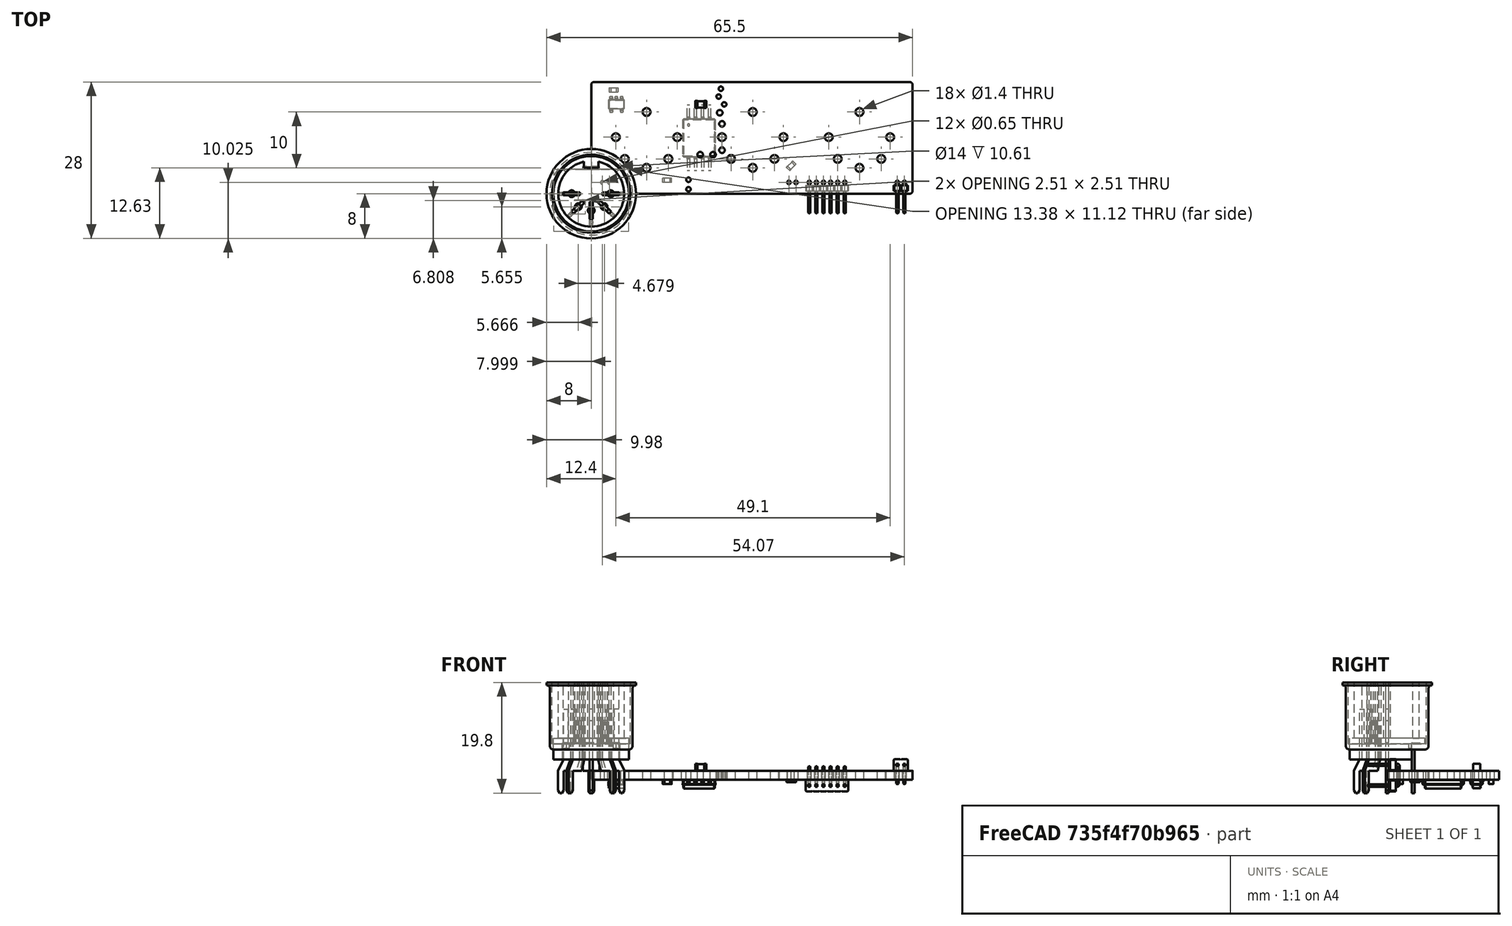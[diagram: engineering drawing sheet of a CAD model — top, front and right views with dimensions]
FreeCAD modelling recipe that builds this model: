
FCSTD DOCUMENT  (FreeCAD 0.20R27422 (Git))
Label: Ultra-midi
License: All rights reserved
LicenseURL: http://en.wikipedia.org/wiki/All_rights_reserved
objects: Part::Feature×30, App::Link×16, App::Part×8, PartDesign::CoordinateSystem×1, Sketcher::SketchObject×1
note: 32 computed .brp shape members not serialized (recipe doc carries the construction recipe); baked Part::Feature solids carry a one-line shape summary decoded from their .brp

FEATURE [PartDesign::CoordinateSystem] Local_CS_69dd
  AttacherType = Attacher::AttachEngine3D
FEATURE [Part::Feature] Pcb_69dd
  Placement = pos=(-116,98,0) rot=(0,0,1;0rad)
  shape: bbox 57.5 x 20 x 1.6 mm, 50 faces (baked)
FEATURE [Sketcher::SketchObject] PCB_Sketch_69dd
  FullyConstrained = false
  sketch-geometry (18):
    g0: LineSegment StartX=57 StartY=20 StartZ=0 EndX=0.5 EndY=20 EndZ=0
    g1: LineSegment StartX=8e-16 StartY=19.5 StartZ=0 EndX=0 EndY=0.5 EndZ=0
    g2: LineSegment StartX=57.5 StartY=0.5 StartZ=0 EndX=57.5 EndY=19.5 EndZ=0
    g3: LineSegment StartX=0.5 StartY=0 StartZ=0 EndX=57 EndY=-1.3e-15 EndZ=0
    g4: ArcOfCircle CenterX=57 CenterY=0.500001 CenterZ=0 NormalX=0 NormalY=0 NormalZ=-1 AngleXU=-3.14159 Radius=0.500001 StartAngle=0 EndAngle=1.57079
    g5: ArcOfCircle CenterX=0.500001 CenterY=19.5 CenterZ=0 NormalX=0 NormalY=0 NormalZ=-1 AngleXU=2.66714e-06 Radius=0.500001 StartAngle=0 EndAngle=1.57079
    g6: ArcOfCircle CenterX=0.500001 CenterY=0.500001 CenterZ=0 NormalX=0 NormalY=0 NormalZ=-1 AngleXU=-1.57079 Radius=0.500001 StartAngle=0 EndAngle=1.57079
    g7: ArcOfCircle CenterX=57 CenterY=19.5 CenterZ=0 NormalX=0 NormalY=0 NormalZ=-1 AngleXU=1.5708 Radius=0.500001 StartAngle=0 EndAngle=1.57079
    g8: Circle CenterX=19.5 CenterY=7 CenterZ=0 NormalX=0 NormalY=0 NormalZ=1 AngleXU=0 Radius=0.5
    g9: Circle CenterX=17.4 CenterY=2.5 CenterZ=0 NormalX=0 NormalY=0 NormalZ=1 AngleXU=0 Radius=0.4
    g10: Circle CenterX=23.4 CenterY=7.8 CenterZ=0 NormalX=0 NormalY=0 NormalZ=1 AngleXU=0 Radius=0.5
    g11: Circle CenterX=23.2 CenterY=18.8 CenterZ=0 NormalX=0 NormalY=0 NormalZ=1 AngleXU=0 Radius=0.4
    g12: Circle CenterX=22.8 CenterY=17.4 CenterZ=0 NormalX=0 NormalY=0 NormalZ=1 AngleXU=0 Radius=0.4
    g13: Circle CenterX=23 CenterY=14.5 CenterZ=0 NormalX=0 NormalY=0 NormalZ=1 AngleXU=0 Radius=0.5
    g14: Circle CenterX=23.4 CenterY=12.5 CenterZ=0 NormalX=0 NormalY=0 NormalZ=1 AngleXU=0 Radius=0.5
    g15: Circle CenterX=17.4 CenterY=0.8 CenterZ=0 NormalX=0 NormalY=0 NormalZ=1 AngleXU=0 Radius=0.4
    g16: Circle CenterX=23.8 CenterY=16 CenterZ=0 NormalX=0 NormalY=0 NormalZ=1 AngleXU=0 Radius=0.4
    g17: Circle CenterX=21.8 CenterY=7 CenterZ=0 NormalX=0 NormalY=0 NormalZ=1 AngleXU=0 Radius=0.5
  constraints (8):
    c: Coincident(g1,g6)
    c: Coincident(g1,g5)
    c: Coincident(g3,g6)
    c: Coincident(g0,g5)
    c: Coincident(g3,g4)
    c: Coincident(g0,g7)
    c: Coincident(g2,g4)
    c: Coincident(g2,g7)
FEATURE [App::Part] Board_Geoms_69dd
  Group = -> [Local_CS_69dd,Pcb_69dd,PCB_Sketch_69dd]
  Origin = -> Origin
FEATURE [Part::Feature] Shape  label="J2_PinHeader_1x02_P127mm_Horizontal_337eb045ee12"
  Placement = pos=(56.05,2.025,0) rot=(0,0,-1;1.5708rad)
  shape: bbox 2.54 x 5.7 x 4.5 mm, 58 faces (baked)
FEATURE [Part::Feature] Shape001  label="C6_C_0805_2012Metric_c09b5ff471bc"
  Placement = pos=(19.6,16,0) rot=(0,0,1;0rad)
  shape: bbox 2 x 1.25 x 1.25 mm, 28 faces (baked)
FEATURE [App::Link] J2_PinHeader_1x02_P127mm_Horizontal_337eb045ee12_ln_  label="J1_PinHeader_1x02_P127mm_Horizontal_ae3b6cd6d5c1"
  LinkPlacement = pos=(3.25,2.025,0) rot=(0,0,-1;1.5708rad)
  LinkedObject = -> Shape
  Placement = pos=(3.25,2.025,0) rot=(0,0,-1;1.5708rad)
FEATURE [App::Link] J2_PinHeader_1x02_P127mm_Horizontal_337eb045ee12_ln_001  label="J3_PinHeader_1x02_P127mm_Horizontal_27ee44c8c3d4"
  LinkPlacement = pos=(36.65,2.025,0) rot=(0,0,-1;1.5708rad)
  LinkedObject = -> Shape
  Placement = pos=(36.65,2.025,0) rot=(0,0,-1;1.5708rad)
FEATURE [Part::Feature] Shape002  label="FB3_L_0603_1608Metric_df2c29076625"
  Placement = pos=(13.6,2.4,-1.6) rot=(0,1,0;3.14159rad)
  shape: bbox 1.6 x 0.8 x 0.8 mm, 28 faces (baked)
FEATURE [Part::Feature] Shape003  label="C5_C_0603_1608Metric_0867c8c5745e"
  Placement = pos=(4,18.6,-1.6) rot=(1,0,0;3.14159rad)
  shape: bbox 1.6 x 0.8 x 0.8 mm, 28 faces (baked)
FEATURE [Part::Feature] Shape004  label="R5_R_0603_1608Metric_8c8bab43711c"
  Placement = pos=(35.8,5,-1.6) rot=(0.92388,0.382683,0;3.14159rad)
  shape: bbox 1.697 x 1.697 x 0.45 mm, 26 faces (baked)
FEATURE [Part::Feature] Shape005  label="J4_PinHeader_1x06_P127mm_Horizontal_489f8f595e1f"
  Placement = pos=(39.025,2.025,-1.6) rot=(0.707107,-0.707107,0;3.14159rad)
  shape: bbox 7.62 x 5.7 x 4.5 mm, 166 faces (baked)
FEATURE [App::Link] FB3_L_0603_1608Metric_df2c29076625_ln_  label="FB1_L_0603_1608Metric_149065dd4c7b"
  LinkPlacement = pos=(36,7.4,-1.6) rot=(0.92388,0.382683,0;3.14159rad)
  LinkedObject = -> Shape002
  Placement = pos=(36,7.4,-1.6) rot=(0.92388,0.382683,0;3.14159rad)
FEATURE [Part::Feature] Shape006  label="U1_SSO_8_68x59mm_P127mm_Clearance8mm_cd01ce0f9bbe"
  Placement = pos=(19.3,10,-1.6) rot=(0.707107,-0.707107,0;3.14159rad)
  shape: bbox 5.9 x 11.7 x 1.6 mm, 156 faces (baked)
FEATURE [Part::Feature] Shape007  label="U2_SOT_23_5_2942c334eb8a"
  Placement = pos=(4.5,16,-1.6) rot=(0.707107,-0.707107,0;3.14159rad)
  shape: bbox 2.9 x 2.8 x 1.55 mm, 109 faces (baked)
FEATURE [App::Link] R5_R_0603_1608Metric_8c8bab43711c_ln_  label="R4_R_0603_1608Metric_3ff6b89587b2"
  LinkPlacement = pos=(8,10,-1.6) rot=(0.707107,0.707107,0;3.14159rad)
  LinkedObject = -> Shape004
  Placement = pos=(8,10,-1.6) rot=(0.707107,0.707107,0;3.14159rad)
FEATURE [App::Link] C5_C_0603_1608Metric_0867c8c5745e_ln_  label="C2_C_0603_1608Metric_22715801060e"
  LinkPlacement = pos=(10.8,8.2,-1.6) rot=(1,0,0;3.14159rad)
  LinkedObject = -> Shape003
  Placement = pos=(10.8,8.2,-1.6) rot=(1,0,0;3.14159rad)
FEATURE [App::Link] C6_C_0805_2012Metric_c09b5ff471bc_ln_  label="C4_C_0805_2012Metric_26a949b8cd84"
  LinkPlacement = pos=(1.8,13,-1.6) rot=(0.707107,0.707107,0;3.14159rad)
  LinkedObject = -> Shape001
  Placement = pos=(1.8,13,-1.6) rot=(0.707107,0.707107,0;3.14159rad)
FEATURE [App::Link] R5_R_0603_1608Metric_8c8bab43711c_ln_001  label="R2_R_0603_1608Metric_4e10fd813094"
  LinkPlacement = pos=(49.5,16.5,-1.6) rot=(0.92388,-0.382683,0;3.14159rad)
  LinkedObject = -> Shape004
  Placement = pos=(49.5,16.5,-1.6) rot=(0.92388,-0.382683,0;3.14159rad)
FEATURE [App::Link] FB3_L_0603_1608Metric_df2c29076625_ln_001  label="FB2_L_0603_1608Metric_fe7989b07d85"
  LinkPlacement = pos=(12.8,12.2,-1.6) rot=(0.707107,0.707107,0;3.14159rad)
  LinkedObject = -> Shape002
  Placement = pos=(12.8,12.2,-1.6) rot=(0.707107,0.707107,0;3.14159rad)
FEATURE [App::Link] C5_C_0603_1608Metric_0867c8c5745e_ln_001  label="C1_C_0603_1608Metric_b41121d6c93c"
  LinkPlacement = pos=(46.2,16.3,-1.6) rot=(0.92388,0.382683,0;3.14159rad)
  LinkedObject = -> Shape003
  Placement = pos=(46.2,16.3,-1.6) rot=(0.92388,0.382683,0;3.14159rad)
FEATURE [App::Link] R5_R_0603_1608Metric_8c8bab43711c_ln_002  label="R7_R_0603_1608Metric_dfa80113c302"
  LinkPlacement = pos=(27,1.8,-1.6) rot=(0,1,0;3.14159rad)
  LinkedObject = -> Shape004
  Placement = pos=(27,1.8,-1.6) rot=(0,1,0;3.14159rad)
FEATURE [App::Link] FB3_L_0603_1608Metric_df2c29076625_ln_002  label="FB4_L_0603_1608Metric_f99d6db0d256"
  LinkPlacement = pos=(54.8,6.2,-1.6) rot=(0.707107,-0.707107,0;3.14159rad)
  LinkedObject = -> Shape002
  Placement = pos=(54.8,6.2,-1.6) rot=(0.707107,-0.707107,0;3.14159rad)
FEATURE [App::Link] FB3_L_0603_1608Metric_df2c29076625_ln_003  label="FB5_L_0603_1608Metric_030844127197"
  LinkPlacement = pos=(25,3.4,-1.6) rot=(0,1,0;3.14159rad)
  LinkedObject = -> Shape002
  Placement = pos=(25,3.4,-1.6) rot=(0,1,0;3.14159rad)
FEATURE [App::Link] R5_R_0603_1608Metric_8c8bab43711c_ln_003  label="R3_R_0603_1608Metric_b0f0240fa3c2"
  LinkPlacement = pos=(14.6,14.8,-1.6) rot=(0,1,0;3.14159rad)
  LinkedObject = -> Shape004
  Placement = pos=(14.6,14.8,-1.6) rot=(0,1,0;3.14159rad)
FEATURE [App::Link] R5_R_0603_1608Metric_8c8bab43711c_ln_004  label="R6_R_0603_1608Metric_639142cc7455"
  LinkPlacement = pos=(33.2,14.6,-1.6) rot=(0,1,0;3.14159rad)
  LinkedObject = -> Shape004
  Placement = pos=(33.2,14.6,-1.6) rot=(0,1,0;3.14159rad)
FEATURE [App::Link] R5_R_0603_1608Metric_8c8bab43711c_ln_005  label="R1_R_0603_1608Metric_cbd55fb59e40"
  LinkPlacement = pos=(53.2,3,-1.6) rot=(0.707107,0.707107,0;3.14159rad)
  LinkedObject = -> Shape004
  Placement = pos=(53.2,3,-1.6) rot=(0.707107,0.707107,0;3.14159rad)
FEATURE [App::Link] C5_C_0603_1608Metric_0867c8c5745e_ln_002  label="C3_C_0603_1608Metric_cf41ac51516b"
  LinkPlacement = pos=(33.1375,16.2,-1.6) rot=(1,0,0;3.14159rad)
  LinkedObject = -> Shape003
  Placement = pos=(33.1375,16.2,-1.6) rot=(1,0,0;3.14159rad)
FEATURE [App::Part] Bot_69dd
  Group = -> [Shape002,Shape003,Shape004,Shape005,FB3_L_0603_1608Metric_df2c29076625_ln_,Shape006,Shape007,R5_R_0603_1608Metric_8c8bab43711c_ln_,C5_C_0603_1608Metric_0867c8c5745e_ln_,C6_C_0805_2012Metric_c09b5ff471bc_ln_,R5_R_0603_1608Metric_8c8bab43711c_ln_001,FB3_L_0603_1608Metric_df2c29076625_ln_001,C5_C_0603_1608Metric_0867c8c5745e_ln_001,R5_R_0603_1608Metric_8c8bab43711c_ln_002,+6 more]
  Origin = -> Origin004
FEATURE [Part::Feature] Part__Feature  label="Casing"
  shape: bbox 18.09 x 18.09 x 19.8 mm, 30 faces (baked)
FEATURE [Part::Feature] Part__Feature001  label="Plastic"
  Placement = pos=(0,0,0) rot=(0,0,1;1.5708rad)
  shape: bbox 13.5 x 13.5 x 13.8 mm, 83 faces (baked)
FEATURE [Part::Feature] Part__Feature002  label="Pin-contact1"
  Placement = pos=(0,0,-4) rot=(0,0,1;0rad)
  shape: bbox 3.9 x 0.55 x 15 mm, 20 faces (baked)
FEATURE [Part::Feature] Part__Feature003  label="Pin-contact002"
  Placement = pos=(0,0,-4) rot=(0,0,1;1.5708rad)
  shape: bbox 0.55 x 3.9 x 15 mm, 20 faces (baked)
FEATURE [Part::Feature] Part__Feature004  label="Pin-contact003"
  Placement = pos=(0,0,-4) rot=(0,0,1;3.14159rad)
  shape: bbox 3.9 x 0.55 x 15 mm, 20 faces (baked)
FEATURE [Part::Feature] Part__Feature005  label="Pin-contact004"
  Placement = pos=(0,0,-4) rot=(0,0,1;0.785398rad)
  shape: bbox 3.147 x 3.147 x 15 mm, 20 faces (baked)
FEATURE [Part::Feature] Part__Feature006  label="Pin-contact005"
  Placement = pos=(0,0,-4) rot=(0,0,1;2.35619rad)
  shape: bbox 3.147 x 3.147 x 15 mm, 20 faces (baked)
FEATURE [App::Part] CUI_SD_50BV
  Group = -> [Part__Feature,Part__Feature001,Part__Feature002,Part__Feature003,Part__Feature004,Part__Feature005,Part__Feature006]
  Origin = -> Origin005
  Placement = pos=(9.9,10,0) rot=(0,0,1;0rad)
FEATURE [Part::Feature] Part__Feature007  label="Casing001"
  shape: bbox 18.09 x 18.09 x 19.8 mm, 30 faces (baked)
FEATURE [Part::Feature] Part__Feature008  label="Pin-contact006"
  Placement = pos=(0,0,-4) rot=(0,0,1;1.5708rad)
  shape: bbox 0.55 x 3.9 x 15 mm, 20 faces (baked)
FEATURE [Part::Feature] Part__Feature009  label="Pin-contact007"
  Placement = pos=(0,0,-4) rot=(0,0,1;0rad)
  shape: bbox 3.9 x 0.55 x 15 mm, 20 faces (baked)
FEATURE [Part::Feature] Part__Feature010  label="Plastic001"
  Placement = pos=(0,0,0) rot=(0,0,1;1.5708rad)
  shape: bbox 13.5 x 13.5 x 13.8 mm, 83 faces (baked)
FEATURE [Part::Feature] Part__Feature011  label="Pin-contact008"
  Placement = pos=(0,0,-4) rot=(0,0,1;3.14159rad)
  shape: bbox 3.9 x 0.55 x 15 mm, 20 faces (baked)
FEATURE [Part::Feature] Part__Feature012  label="Pin-contact009"
  Placement = pos=(0,0,-4) rot=(0,0,1;0.785398rad)
  shape: bbox 3.147 x 3.147 x 15 mm, 20 faces (baked)
FEATURE [Part::Feature] Part__Feature013  label="Pin-contact010"
  Placement = pos=(0,0,-4) rot=(0,0,1;2.35619rad)
  shape: bbox 3.147 x 3.147 x 15 mm, 20 faces (baked)
FEATURE [App::Part] CUI_SD_50BV001
  Group = -> [Part__Feature007,Part__Feature010,Part__Feature009,Part__Feature008,Part__Feature011,Part__Feature012,Part__Feature013]
  Origin = -> Origin006
  Placement = pos=(28.9,10,0) rot=(0,0,1;0rad)
FEATURE [Part::Feature] Part__Feature014  label="Casing002"
  shape: bbox 18.09 x 18.09 x 19.8 mm, 30 faces (baked)
FEATURE [Part::Feature] Part__Feature015  label="Pin-contact011"
  Placement = pos=(0,0,-4) rot=(0,0,1;1.5708rad)
  shape: bbox 0.55 x 3.9 x 15 mm, 20 faces (baked)
FEATURE [Part::Feature] Part__Feature016  label="Pin-contact012"
  Placement = pos=(0,0,-4) rot=(0,0,1;0rad)
  shape: bbox 3.9 x 0.55 x 15 mm, 20 faces (baked)
FEATURE [Part::Feature] Part__Feature017  label="Plastic002"
  Placement = pos=(0,0,0) rot=(0,0,1;1.5708rad)
  shape: bbox 13.5 x 13.5 x 13.8 mm, 83 faces (baked)
FEATURE [Part::Feature] Part__Feature018  label="Pin-contact013"
  Placement = pos=(0,0,-4) rot=(0,0,1;3.14159rad)
  shape: bbox 3.9 x 0.55 x 15 mm, 20 faces (baked)
FEATURE [Part::Feature] Part__Feature019  label="Pin-contact014"
  Placement = pos=(0,0,-4) rot=(0,0,1;0.785398rad)
  shape: bbox 3.147 x 3.147 x 15 mm, 20 faces (baked)
FEATURE [Part::Feature] Part__Feature020  label="Pin-contact015"
  Placement = pos=(0,0,-4) rot=(0,0,1;2.35619rad)
  shape: bbox 3.147 x 3.147 x 15 mm, 20 faces (baked)
FEATURE [App::Part] CUI_SD_50BV002
  Group = -> [Part__Feature014,Part__Feature017,Part__Feature016,Part__Feature015,Part__Feature018,Part__Feature019,Part__Feature020]
  Origin = -> Origin007
  Placement = pos=(48,10,0) rot=(0,0,1;0rad)
FEATURE [App::Part] Top_69dd
  Group = -> [Shape,Shape001,J2_PinHeader_1x02_P127mm_Horizontal_337eb045ee12_ln_,J2_PinHeader_1x02_P127mm_Horizontal_337eb045ee12_ln_001,CUI_SD_50BV,CUI_SD_50BV001,CUI_SD_50BV002]
  Origin = -> Origin003
FEATURE [App::Part] Step_Models_69dd
  Group = -> [Top_69dd,Bot_69dd]
  Origin = -> Origin002
FEATURE [App::Part] Board_69dd  label="Ultra-Midi"
  Group = -> [Board_Geoms_69dd,Step_Models_69dd]
  Origin = -> Origin001
